annotation { "Feature Type Name" : "Feature", "Feature Type Description" : "" }
export const myFeature = defineFeature(function(context is Context, id is Id, definition is map)
    precondition{}
    {
        {
            var Q0;
            Q0=qCreatedBy(makeId("Top.planeOp"),FACE);
            var sketch = newSketch(context, id + "F0", { "sketchPlane" : qUnion([Q0])});
            skLineSegment(sketch, "E0.bottom", {"start": v(2.5, -5) * mm, "end": v(-2.5, -5) * mm});
            skLineSegment(sketch, "E0.top", {"start": v(2.5, 5) * mm, "end": v(-2.5, 5) * mm});
            skLineSegment(sketch, "E0.left", {"start": v(2.5, -5) * mm, "end": v(2.5, 5) * mm});
            skLineSegment(sketch, "E0.right", {"start": v(-2.5, -5) * mm, "end": v(-2.5, 5) * mm});
            skPoint(sketch, "E0.middle", {"position": v(0, 0) * mm});
            skLineSegment(sketch, "E1", {"start": v(2.5, 5) * mm, "end": v(2.5, 2.5) * mm});
            skLineSegment(sketch, "E2.bottom", {"start": v(2.5, 2.5) * mm, "end": v(7.5, 2.5) * mm});
            skLineSegment(sketch, "E2.top", {"start": v(2.5, 0) * mm, "end": v(7.5, 0) * mm});
            skLineSegment(sketch, "E2.left", {"start": v(2.5, 2.5) * mm, "end": v(2.5, 0) * mm});
            skLineSegment(sketch, "E2.right", {"start": v(7.5, 2.5) * mm, "end": v(7.5, 0) * mm});
            skLineSegment(sketch, "E3.bottom", {"start": v(-2.5, 5) * mm, "end": v(0.5, 5) * mm});
            skLineSegment(sketch, "E3.top", {"start": v(-2.5, 17) * mm, "end": v(0.5, 17) * mm});
            skLineSegment(sketch, "E3.left", {"start": v(-2.5, 5) * mm, "end": v(-2.5, 17) * mm});
            skLineSegment(sketch, "E3.right", {"start": v(0.5, 5) * mm, "end": v(0.5, 17) * mm});
            skCircle(sketch, "E4", {"center": v(0, 0) * mm, "radius": 2 * mm});
            skSolve(sketch);
        }
        {
            var Q0;
            Q0=makeQuery(id+"F0.imprint","IMPRINT",FACE,{"disambiguationData":[TD([[makeQuery(id+"F0.imprint","IMPRINT",EDGE,{"derivedFrom":sQuery(id+"F0.wireOp",EDGE,"E0.bottom")}),-1.0]])]});
            var Q1;
            Q1=makeQuery(id+"F0.imprint","IMPRINT",FACE,{"disambiguationData":[TD([[makeQuery(id+"F0.imprint","IMPRINT",EDGE,{"derivedFrom":sQuery(id+"F0.wireOp",EDGE,"E3.bottom")}),1.0]])]});
            var Q2;
            Q2=makeQuery(id+"F0.imprint","IMPRINT",FACE,{"disambiguationData":[TD([[makeQuery(id+"F0.imprint","IMPRINT",EDGE,{"derivedFrom":sQuery(id+"F0.wireOp",EDGE,"E2.bottom")}),-1.0]])]});
            extrude(context, id + "F1", {"entities" : qUnion([Q0, Q1, Q2]), "depth" : 8 * mm, "offsetDistance" : 25 * mm});
        }
        {
            var Q0;
            Q0=makeQuery(id+"F1.opExtrude","CAP_FACE",FACE,{"disambiguationData":[OSD([sQuery(id+"F0.wireOp",EDGE,"E0.bottom"),sQuery(id+"F0.wireOp",EDGE,"E0.top"),sQuery(id+"F0.wireOp",EDGE,"E0.left"),sQuery(id+"F0.wireOp",EDGE,"E0.right"),sQuery(id+"F0.wireOp",EDGE,"E1"),sQuery(id+"F0.wireOp",EDGE,"E2.bottom"),sQuery(id+"F0.wireOp",EDGE,"E2.top"),sQuery(id+"F0.wireOp",EDGE,"E2.right"),sQuery(id+"F0.wireOp",EDGE,"E3.top"),sQuery(id+"F0.wireOp",EDGE,"E3.left"),sQuery(id+"F0.wireOp",EDGE,"E3.right"),sQuery(id+"F0.wireOp",EDGE,"E4")])],"isStart":false});
            var sketch = newSketch(context, id + "F2", { "sketchPlane" : qUnion([Q0])});
            skLineSegment(sketch, "E5", {"start": v(-2.5, -5) * mm, "end": v(-1.5, -5) * mm});
            skLineSegment(sketch, "E6", {"start": v(-1.5, -5) * mm, "end": v(-1.5, -4) * mm});
            skCircle(sketch, "E7", {"center": v(-1.5, -4) * mm, "radius": 1.75 * mm});
            skCircle(sketch, "E8", {"center": v(-1.5, -4) * mm, "radius": 2.5 * mm});
            skSolve(sketch);
        }
        {
            var Q0;
            {var subQ1=makeQuery(id+"F1.opExtrude","CAP_EDGE",EDGE,{"disambiguationData":[OSD([sQuery(id+"F0.wireOp",EDGE,"E0.bottom")])],"isStart":false});var subQ5=sQuery(id+"F2.wireOp",EDGE,"E8");var subQ6=makeQuery(id+"F2.imprint","INTERSECT",VERTEX,{"derivedFrom":[subQ1,subQ5]});Q0=makeQuery(id+"F2.imprint","IMPRINT",FACE,{"disambiguationData":[TD([[makeQuery(id+"F2.imprint","IMPRINT",EDGE,{"disambiguationData":[TD([[subQ6,-1.0]])],"derivedFrom":subQ5}),1.0]])]});}
            extrude(context, id + "F3", {"entities" : qUnion([Q0]), "operationType" : NewBodyOperationType.REMOVE, "oppositeDirection" : true, "depth" : 5 * mm, "offsetDistance" : 25 * mm});
        }
    });